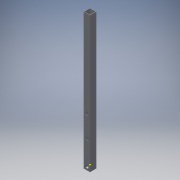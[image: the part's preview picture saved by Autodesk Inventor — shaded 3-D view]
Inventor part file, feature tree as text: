
AUTODESK INVENTOR PART (.ipt)
format: ipt  version: 2016 (Build 200138000, 138)  size: 133,632 bytes
history: native  units: in
note: dims shown in document units (in); Inventor stores cm internally (conversion verified against a paired STEP export)
features: sketch x6, extrude x5
ambient origin geometry x8: Origin, YZ Plane, XZ Plane, XY Plane, X Axis, Y Axis, Z Axis, Center Point
bodies: Solid1 (feature_tree)
feature tree (11):
  extrude  "Extrusion1"  Depth=1.0in
  sketch  "Sketch3"  dims[d2=0.0625in d3=16.5in d4=0.0in]
  extrude  "Extrusion3"  Depth=0.0625in TaperAngle=0.0deg
  extrude  "Extrusion4"  Depth=1.0in TaperAngle=0.0deg
  extrude  "Extrusion6"  Depth=1.0in TaperAngle=0.0deg
  extrude  "Extrusion7"  Depth=1.0in TaperAngle=0.0deg
  sketch  "Sketch1"  dims[d0=1.0in d1=1.0in]
  sketch  "Sketch4"  dims[d8=0.5in d10=1.0in d11=0.0in]
  sketch  "Sketch5"  dims[d12=0.5in d13=1.0in d14=0.0in]
  sketch  "Sketch7"  dims[d15=10.5in d21=1.0in d22=0.0in]
  sketch  "Sketch8"  dims[d23=0.5in d24=0.5in d25=1.0in d26=0.0in d27=0.5in d28=0.5in d29=0.5in]
